# Revit family: INT-3-K
name_source: partatom
category: Lighting Fixtures
revit_build: Autodesk Revit 2014 (Build: 20130308_1515(x64)
units: mm (PartAtom-declared; Revit-internal decimal feet)

## types (1)
- INT
    Angle Tilt = 45°
    Apparent Load = 15 VA
    Assembly Code = D5020200
    Connector Description = Lighting Connector
    Default Elevation = 48 "
    Description = Intent
    Features = Architectural linear product for wall and ground mounting
applications such as sign lighting, wall washing, wall grazing, and
building accent lighting
• IP66 rated product with linear run capabilities
• Lumen range from 657 to 3,271 lm
    Fixture distribution = Direct
    Glass = Hubbell - Glass
    Height = 4 "
    Housing Material = Paint - Hubbell - Basic Black Textured
    Lamp = LED
    Length = 24 "
    Load Classification = Lighting
    Manufacturer = Kim Lighting
    Model = INT-3-K
    Mounting = Paint - Hubbell - Light Silver
    Power Factor = 1
    Product Family URL = https://www.hubbell.com
    Product RGWB URL = https://www.hubbell.com
    Product White URL = https://www.hubbell.com
    Reflector Finish = Hubbell - White Glass
    URL = https://www.hubbell.com
    Voltage = 120 V
    Warranty = 5 years Warranty
    Wattage Comments = 15W
    Watts = 15 W
    Width = 3.875 "
    Wings = Paint - Hubbell - Light Silver
    zz Angle = 45°

## geometry (parser evidence)
native form markers: Sweep x9
no freeform markers — native parametric forms only
